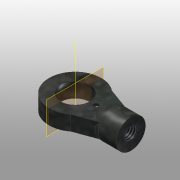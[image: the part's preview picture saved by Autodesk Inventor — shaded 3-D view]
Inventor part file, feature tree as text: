
AUTODESK INVENTOR PART (.ipt)
format: ipt  version: 2016 (Build 200138000, 138)  size: 156,160 bytes
history: native  units: mm
features: sketch x4, revolve x2, hole x2, projected_geometry x2, extrude x1, plane x1, other x1
ambient origin geometry x8: Origin, YZ Plane, XZ Plane, XY Plane, X Axis, Y Axis, Z Axis, Center Point
bodies: Solid1 (feature_tree)
feature tree (13):
  revolve  "Revolution1"  [1 undecoded]
  extrude  "Extrusion1"  Depth=10.2mm
  hole  "Hole1"  [1 undecoded]
  plane  "Work Plane1"
  revolve  "Revolution2"  [1 undecoded]
  hole  "Hole2"  [1 undecoded]
  sketch  "Sketch1"  dims[d0=2.85mm d1=3.5mm]
  sketch  "Sketch2"  dims[d2=90.0deg d3=10.2mm]
  other  "Work Axis1"
  sketch  "Sketch3"  dims[d4=10.9mm d7=8.0mm]
  sketch  "Sketch4"  dims[d10=2.9mm d11=0.0mm d12=19.198622mm d13=19.198622mm d23=10.0mm d24=10.0mm d16=2.459mm d17=5.0mm d18=4.0mm d19=2.0mm d20=90.0deg d21=6.0mm d22=20.594885mm d25=0.0mm d26=6.4mm d27=90.0deg d28=1.0mm d29=1.0mm d30=4.0mm d31=2.0mm d32=90.0deg d33=0.5mm d34=20.594885mm]
  projected_geometry  "Project Cut Edges1"
  projected_geometry  "Project Cut Edges2"
note: 4 required parameter values undecoded (feature->parameter linkage not recoverable at this tier; creation-order binding heuristic only, values carry confidence <= 0.55)